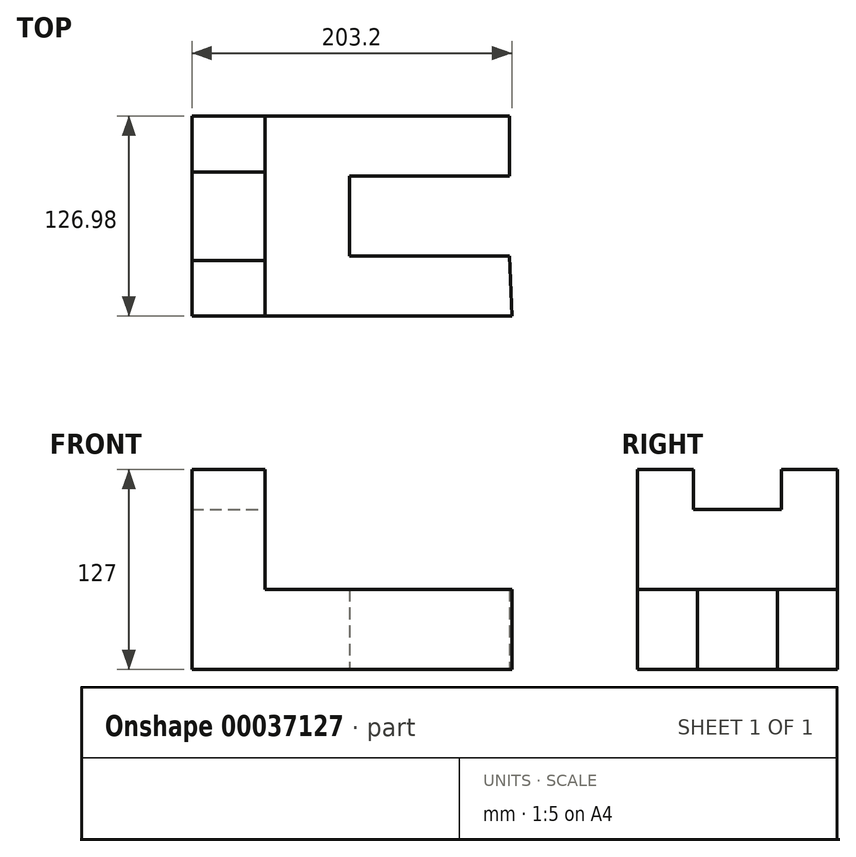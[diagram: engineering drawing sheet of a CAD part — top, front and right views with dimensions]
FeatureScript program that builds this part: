
annotation { "Feature Type Name" : "Feature", "Feature Type Description" : "" }
export const myFeature = defineFeature(function(context is Context, id is Id, definition is map)
    precondition{}
    {
        {
            var Q0;
            Q0=qCreatedBy(makeId("Top.planeOp"),FACE);
            var sketch = newSketch(context, id + "F0", { "sketchPlane" : qUnion([Q0])});
            skLineSegment(sketch, "E0", {"start": v(-98.6, 29) * mm, "end": v(103.25, 29) * mm});
            skLineSegment(sketch, "E1", {"start": v(-98.6, 29) * mm, "end": v(-98.6, -97.97) * mm});
            skLineSegment(sketch, "E2", {"start": v(-98.6, -97.97) * mm, "end": v(104.6, -97.97) * mm});
            skLineSegment(sketch, "E3", {"start": v(103.25, 29) * mm, "end": v(103.25, -9.1) * mm});
            skLineSegment(sketch, "E4", {"start": v(103.25, -9.1) * mm, "end": v(1.65, -9.1) * mm});
            skLineSegment(sketch, "E5", {"start": v(1.65, -9.1) * mm, "end": v(1.65, -59.9) * mm});
            skLineSegment(sketch, "E6", {"start": v(1.65, -59.9) * mm, "end": v(103.25, -59.9) * mm});
            skLineSegment(sketch, "E7", {"start": v(103.25, -59.9) * mm, "end": v(104.6, -97.97) * mm});
            skSolve(sketch);
        }
        {
            var Q0;
            Q0=makeQuery(id+"F0.imprint","IMPRINT",FACE,{"disambiguationData":[TD([[makeQuery(id+"F0.imprint","IMPRINT",EDGE,{"derivedFrom":sQuery(id+"F0.wireOp",EDGE,"E0")}),-1.0]])]});
            extrude(context, id + "F1", {"entities" : qUnion([Q0]), "depth" : 50.8 * mm});
        }
        {
            var Q0;
            Q0=makeQuery(id+"F1.opExtrude","CAP_FACE",FACE,{"disambiguationData":[OSD([sQuery(id+"F0.wireOp",EDGE,"E0"),sQuery(id+"F0.wireOp",EDGE,"E1"),sQuery(id+"F0.wireOp",EDGE,"E2"),sQuery(id+"F0.wireOp",EDGE,"E3"),sQuery(id+"F0.wireOp",EDGE,"E4"),sQuery(id+"F0.wireOp",EDGE,"E5"),sQuery(id+"F0.wireOp",EDGE,"E6"),sQuery(id+"F0.wireOp",EDGE,"E7")])],"isStart":false});
            var sketch = newSketch(context, id + "F2", { "sketchPlane" : qUnion([Q0])});
            skLineSegment(sketch, "E8", {"start": v(-52.15, 29) * mm, "end": v(-52.15, -97.97) * mm});
            skLineSegment(sketch, "E9", {"start": v(-52.15, -97.97) * mm, "end": v(-98.6, -97.97) * mm});
            skLineSegment(sketch, "E10", {"start": v(-98.6, -97.97) * mm, "end": v(-98.6, 29) * mm});
            skLineSegment(sketch, "E11", {"start": v(-98.6, 29) * mm, "end": v(-52.15, 29) * mm});
            skSolve(sketch);
        }
        {
            var Q0;
            Q0=makeQuery(id+"F2.imprint","IMPRINT",FACE,{"disambiguationData":[TD([[makeQuery(id+"F2.imprint","IMPRINT",EDGE,{"derivedFrom":sQuery(id+"F2.wireOp",EDGE,"E8")}),-1.0]])]});
            extrude(context, id + "F3", {"entities" : qUnion([Q0]), "operationType" : NewBodyOperationType.ADD, "depth" : 76.2 * mm});
        }
        {
            var Q0;
            Q0=makeQuery(id+"F3.opExtrude","SWEPT_FACE",FACE,{"disambiguationData":[OSD([sQuery(id+"F2.wireOp",EDGE,"E8")])]});
            var sketch = newSketch(context, id + "F4", { "sketchPlane" : qUnion([Q0])});
            skLineSegment(sketch, "E12", {"start": v(-62.68, 127) * mm, "end": v(-62.68, 101.6) * mm});
            skLineSegment(sketch, "E13", {"start": v(-62.68, 101.6) * mm, "end": v(-6.53, 101.6) * mm});
            skLineSegment(sketch, "E14", {"start": v(-6.53, 101.6) * mm, "end": v(-6.53, 127) * mm});
            skLineSegment(sketch, "E15", {"start": v(-6.53, 127) * mm, "end": v(-62.68, 127) * mm});
            skSolve(sketch);
        }
        {
            var Q0;
            Q0=makeQuery(id+"F4.imprint","IMPRINT",FACE,{"disambiguationData":[TD([[makeQuery(id+"F4.imprint","IMPRINT",EDGE,{"derivedFrom":sQuery(id+"F4.wireOp",EDGE,"E12")}),1.0]])]});
            extrude(context, id + "F5", {"entities" : qUnion([Q0]), "operationType" : NewBodyOperationType.REMOVE, "oppositeDirection" : true, "depth" : 50.8 * mm});
        }
    });
